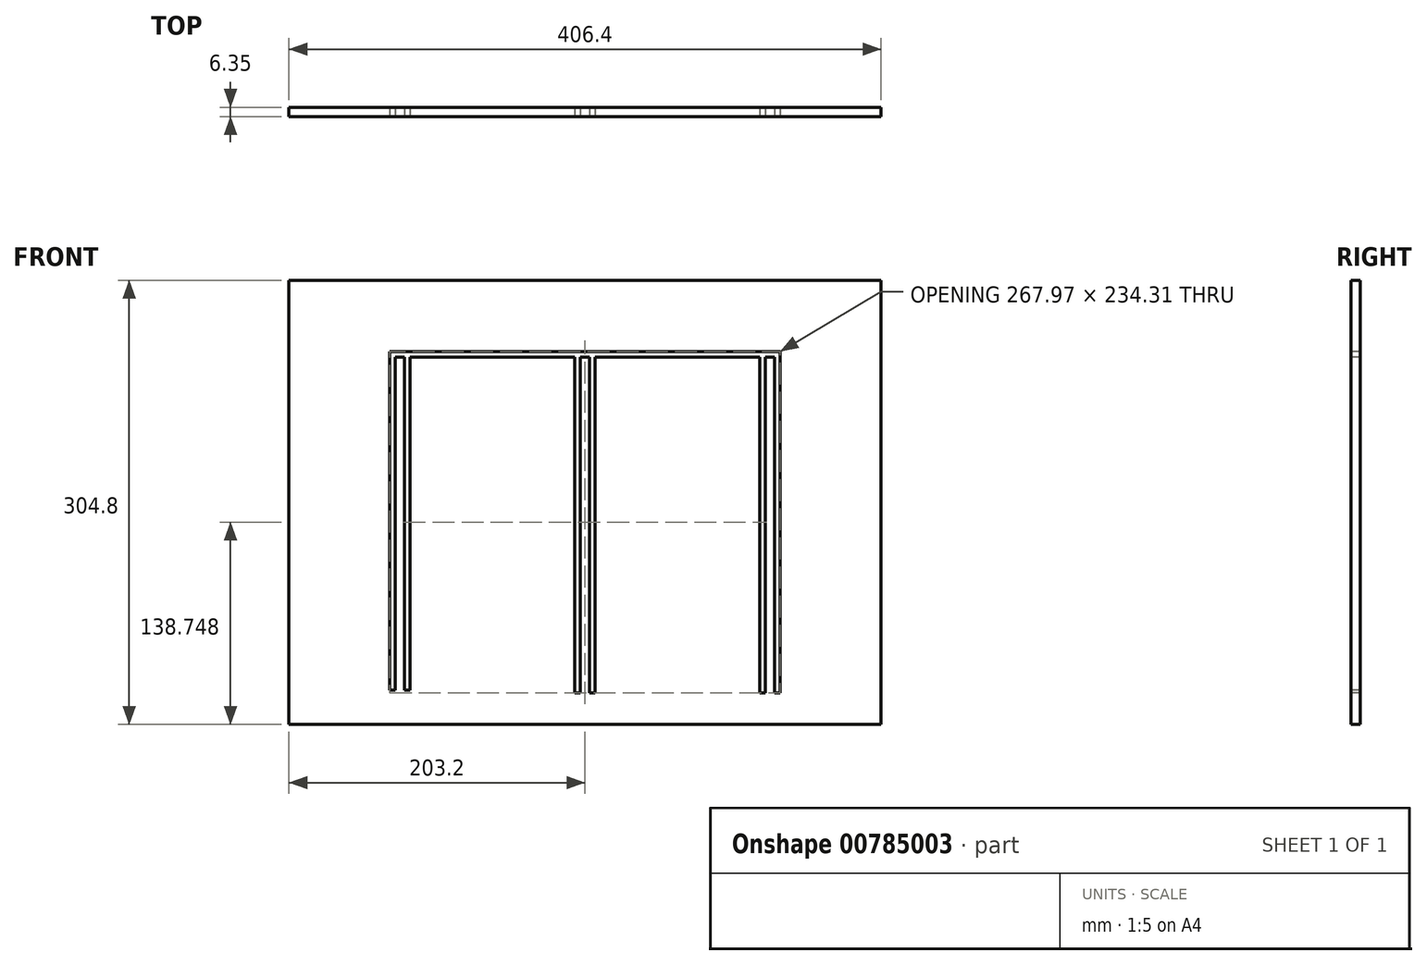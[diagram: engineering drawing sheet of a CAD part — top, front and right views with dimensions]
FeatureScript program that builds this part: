
annotation { "Feature Type Name" : "Feature", "Feature Type Description" : "" }
export const myFeature = defineFeature(function(context is Context, id is Id, definition is map)
    precondition{}
    {
        {
            var Q0;
            Q0=qCreatedBy(makeId("Front.planeOp"),FACE);
            var sketch = newSketch(context, id + "F0", { "sketchPlane" : qUnion([Q0])});
            skLineSegment(sketch, "E0.bottom", {"start": v(203.2, -152.4) * mm, "end": v(-203.2, -152.4) * mm});
            skLineSegment(sketch, "E0.top", {"start": v(203.2, 152.4) * mm, "end": v(-203.2, 152.4) * mm});
            skLineSegment(sketch, "E0.left", {"start": v(203.2, -152.4) * mm, "end": v(203.2, 152.4) * mm});
            skLineSegment(sketch, "E0.right", {"start": v(-203.2, -152.4) * mm, "end": v(-203.2, 152.4) * mm});
            skPoint(sketch, "E0.middle", {"position": v(0, 0) * mm});
            skLineSegment(sketch, "E1.bottom", {"start": v(3.18, 130.8) * mm, "end": v(-3.17, 130.8) * mm});
            skLineSegment(sketch, "E1.top", {"start": v(3.18, -130.8) * mm, "end": v(-3.17, -130.8) * mm});
            skLineSegment(sketch, "E1.left", {"start": v(3.18, 130.8) * mm, "end": v(3.18, -130.8) * mm});
            skLineSegment(sketch, "E1.right", {"start": v(-3.17, 130.8) * mm, "end": v(-3.17, -130.8) * mm});
            skLineSegment(sketch, "E2.bottom", {"start": v(3.18, -130.8) * mm, "end": v(6.99, -130.8) * mm});
            skLineSegment(sketch, "E2.top", {"start": v(3.18, 103.5) * mm, "end": v(6.99, 103.5) * mm});
            skLineSegment(sketch, "E2.left", {"start": v(3.18, -130.8) * mm, "end": v(3.18, 103.5) * mm});
            skLineSegment(sketch, "E2.right", {"start": v(6.99, -130.8) * mm, "end": v(6.99, 103.5) * mm});
            skLineSegment(sketch, "E3.bottom", {"start": v(-3.17, -130.8) * mm, "end": v(-6.98, -130.8) * mm});
            skLineSegment(sketch, "E3.top", {"start": v(-3.17, 103.5) * mm, "end": v(-6.98, 103.5) * mm});
            skLineSegment(sketch, "E3.left", {"start": v(-3.17, -130.8) * mm, "end": v(-3.17, 103.5) * mm});
            skLineSegment(sketch, "E3.right", {"start": v(-6.98, -130.8) * mm, "end": v(-6.98, 103.5) * mm});
            skPoint(sketch, "E4.middle", {"position": v(-127, 10.8) * mm});
            skLineSegment(sketch, "E5.bottom", {"start": v(-123.83, 150.5) * mm, "end": v(-130.18, 150.5) * mm});
            skLineSegment(sketch, "E5.top", {"start": v(-123.82, -128.9) * mm, "end": v(-130.17, -128.9) * mm});
            skLineSegment(sketch, "E5.left", {"start": v(-123.83, 150.5) * mm, "end": v(-123.82, -128.9) * mm});
            skLineSegment(sketch, "E5.right", {"start": v(-130.18, 150.5) * mm, "end": v(-130.17, -128.9) * mm});
            skLineSegment(sketch, "E6.bottom", {"start": v(-123.82, -128.9) * mm, "end": v(-120.02, -128.9) * mm});
            skLineSegment(sketch, "E6.top", {"start": v(-123.83, 103.5) * mm, "end": v(-120.02, 103.5) * mm});
            skLineSegment(sketch, "E6.left", {"start": v(-123.82, -128.9) * mm, "end": v(-123.83, 103.5) * mm});
            skLineSegment(sketch, "E6.right", {"start": v(-120.02, -128.9) * mm, "end": v(-120.02, 103.5) * mm});
            skLineSegment(sketch, "E7.bottom", {"start": v(-130.17, -128.9) * mm, "end": v(-133.98, -128.9) * mm});
            skLineSegment(sketch, "E7.top", {"start": v(-130.18, 103.5) * mm, "end": v(-133.99, 103.5) * mm});
            skLineSegment(sketch, "E7.left", {"start": v(-130.17, -128.9) * mm, "end": v(-130.18, 103.5) * mm});
            skLineSegment(sketch, "E7.right", {"start": v(-133.98, -128.9) * mm, "end": v(-133.99, 103.5) * mm});
            skPoint(sketch, "E8.middle", {"position": v(127, 8.9) * mm});
            skLineSegment(sketch, "E9.bottom", {"start": v(130.18, 148.6) * mm, "end": v(123.83, 148.6) * mm});
            skLineSegment(sketch, "E9.top", {"start": v(130.18, -130.8) * mm, "end": v(123.83, -130.8) * mm});
            skLineSegment(sketch, "E9.left", {"start": v(130.18, 148.6) * mm, "end": v(130.18, -130.8) * mm});
            skLineSegment(sketch, "E9.right", {"start": v(123.83, 148.6) * mm, "end": v(123.83, -130.8) * mm});
            skLineSegment(sketch, "E10.bottom", {"start": v(130.18, -130.8) * mm, "end": v(133.99, -130.8) * mm});
            skLineSegment(sketch, "E10.top", {"start": v(130.18, 103.5) * mm, "end": v(133.99, 103.5) * mm});
            skLineSegment(sketch, "E10.left", {"start": v(130.18, -130.8) * mm, "end": v(130.18, 103.5) * mm});
            skLineSegment(sketch, "E10.right", {"start": v(133.99, -130.8) * mm, "end": v(133.99, 103.5) * mm});
            skLineSegment(sketch, "E11.bottom", {"start": v(123.83, -130.8) * mm, "end": v(120.02, -130.8) * mm});
            skLineSegment(sketch, "E11.top", {"start": v(123.83, 103.5) * mm, "end": v(120.02, 103.5) * mm});
            skLineSegment(sketch, "E11.left", {"start": v(123.83, -130.8) * mm, "end": v(123.83, 103.5) * mm});
            skLineSegment(sketch, "E11.right", {"start": v(120.02, -130.8) * mm, "end": v(120.02, 103.5) * mm});
            skLineSegment(sketch, "E12.bottom", {"start": v(-133.99, 103.5) * mm, "end": v(133.99, 103.5) * mm});
            skLineSegment(sketch, "E12.top", {"start": v(-133.99, 99.7) * mm, "end": v(133.99, 99.7) * mm});
            skLineSegment(sketch, "E12.left", {"start": v(-133.99, 103.5) * mm, "end": v(-133.99, 99.7) * mm});
            skLineSegment(sketch, "E12.right", {"start": v(133.99, 103.5) * mm, "end": v(133.99, 99.7) * mm});
            skSolve(sketch);
        }
        {
            var Q0;
            Q0=makeQuery(id+"F0.imprint","IMPRINT",FACE,{"disambiguationData":[TD([[makeQuery(id+"F0.imprint","IMPRINT",EDGE,{"derivedFrom":sQuery(id+"F0.wireOp",EDGE,"E0.bottom")}),-1.0]])]});
            var Q1;
            Q1=makeQuery(id+"F0.imprint","IMPRINT",FACE,{"disambiguationData":[TD([[makeQuery(id+"F0.imprint","IMPRINT",EDGE,{"derivedFrom":sQuery(id+"F0.wireOp",EDGE,"E5.bottom")}),1.0]])]});
            var Q2;
            Q2=makeQuery(id+"F0.imprint","IMPRINT",FACE,{"disambiguationData":[TD([[makeQuery(id+"F0.imprint","IMPRINT",EDGE,{"derivedFrom":sQuery(id+"F0.wireOp",EDGE,"E1.bottom")}),1.0]])]});
            var Q3;
            {var subQ0=sQuery(id+"F0.wireOp",EDGE,"E5.top");Q3=makeQuery(id+"F0.imprint","IMPRINT",FACE,{"disambiguationData":[TD([[makeQuery(id+"F0.imprint","IMPRINT",EDGE,{"derivedFrom":subQ0}),-1.0]])]});}
            var Q4;
            {var subQ0=sQuery(id+"F0.wireOp",EDGE,"E1.top");Q4=makeQuery(id+"F0.imprint","IMPRINT",FACE,{"disambiguationData":[TD([[makeQuery(id+"F0.imprint","IMPRINT",EDGE,{"derivedFrom":subQ0}),-1.0]])]});}
            var Q5;
            Q5=makeQuery(id+"F0.imprint","IMPRINT",FACE,{"disambiguationData":[TD([[makeQuery(id+"F0.imprint","IMPRINT",EDGE,{"derivedFrom":sQuery(id+"F0.wireOp",EDGE,"E9.bottom")}),1.0]])]});
            var Q6;
            {var subQ0=sQuery(id+"F0.wireOp",EDGE,"E9.top");Q6=makeQuery(id+"F0.imprint","IMPRINT",FACE,{"disambiguationData":[TD([[makeQuery(id+"F0.imprint","IMPRINT",EDGE,{"derivedFrom":subQ0}),-1.0]])]});}
            extrude(context, id + "F1", {"entities" : qUnion([Q0, Q1, Q2, Q3, Q4, Q5, Q6]), "oppositeDirection" : true, "depth" : 6.35 * mm, "offsetDistance" : 25.4 * mm});
        }
    });
